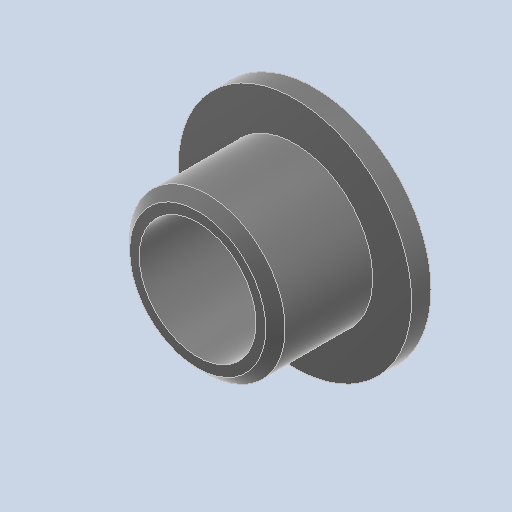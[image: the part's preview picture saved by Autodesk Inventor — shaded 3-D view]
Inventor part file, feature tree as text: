
AUTODESK INVENTOR PART (.ipt)
format: ipt  version: 2023 (Build 270158000, 158)  size: 117,248 bytes
history: native  units: mm
features: other x3, sketch x2
ambient origin geometry x8: Origin, YZ Plane, XZ Plane, XY Plane, X Axis, Y Axis, Z Axis, Center Point
bodies: Solid1 (feature_tree)
feature tree (5):
  other  "w5f6-12a.ipt"
  other  "Solid1::w5f6-12a.ipt"
  other  "TaggingFeature1"
  sketch  "Sketch1"  dims[d0=10.0mm]
  sketch  "Sketch2"
